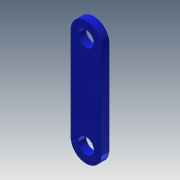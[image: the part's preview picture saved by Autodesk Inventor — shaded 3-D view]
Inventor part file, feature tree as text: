
AUTODESK INVENTOR PART (.ipt)
format: ipt  version: 2015 (Build 190159000, 159)  size: 97,792 bytes
history: native  units: mm
features: sketch x6, extrude x2
ambient origin geometry x8: Origin, YZ Plane, XZ Plane, XY Plane, X Axis, Y Axis, Z Axis, Center Point
bodies: Solid1 (feature_tree)
feature tree (8):
  extrude  "Extrusion1"  Depth=6.0mm
  extrude  "Extrusion2"  Depth=1.5mm TaperAngle=0.0deg
  sketch  "Sketch3"  dims[d5=3.0mm]
  sketch  "Sketch4"  dims[d6=3.0mm]
  sketch  "Sketch5"  dims[d7=2.0mm d8=0.0mm]
  sketch  "Sketch6"
  sketch  "Sketch1"  dims[d0=6.0mm d1=18.0mm]
  sketch  "Sketch2"  dims[d2=6.0mm d3=1.5mm d4=0.0mm]
